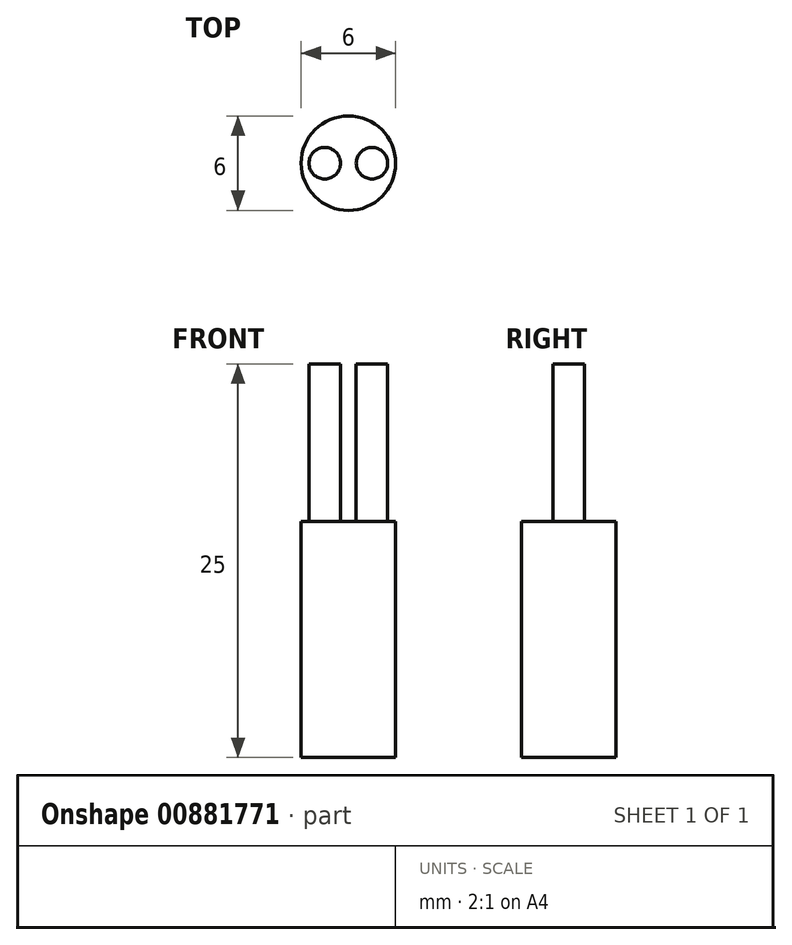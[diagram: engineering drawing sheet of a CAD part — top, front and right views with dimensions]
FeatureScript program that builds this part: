
annotation { "Feature Type Name" : "Feature", "Feature Type Description" : "" }
export const myFeature = defineFeature(function(context is Context, id is Id, definition is map)
    precondition{}
    {
        {
            var Q0;
            Q0=qCreatedBy(makeId("Top.planeOp"),FACE);
            var sketch = newSketch(context, id + "F0", { "sketchPlane" : qUnion([Q0])});
            skCircle(sketch, "E0", {"center": v(0, 0) * mm, "radius": 3 * mm});
            skSolve(sketch);
        }
        {
            var Q0;
            Q0=qSketchRegion(id+"F0",true);
            extrude(context, id + "F1", {"entities" : qUnion([Q0]), "depth" : 15 * mm, "offsetDistance" : 25 * mm});
        }
        {
            var Q0;
            Q0=makeQuery(id+"F1.opExtrude","CAP_FACE",FACE,{"disambiguationData":[OSD([sQuery(id+"F0.wireOp",EDGE,"E0")])],"isStart":false});
            var sketch = newSketch(context, id + "F2", { "sketchPlane" : qUnion([Q0])});
            skCircle(sketch, "E1", {"center": v(-1.5, 0) * mm, "radius": 1 * mm});
            skCircle(sketch, "E2", {"center": v(1.5, 0) * mm, "radius": 1 * mm});
            skLineSegment(sketch, "E3", {"start": v(0, 3.38) * mm, "end": v(0, -3.42) * mm, "construction": true});
            skLineSegment(sketch, "E4", {"start": v(-3.28, 0) * mm, "end": v(3.47, 0) * mm, "construction": true});
            skSolve(sketch);
        }
        {
            var Q0;
            Q0=qSketchRegion(id+"F2",true);
            extrude(context, id + "F3", {"entities" : qUnion([Q0]), "operationType" : NewBodyOperationType.ADD, "depth" : 10 * mm, "offsetDistance" : 25 * mm});
        }
    });
